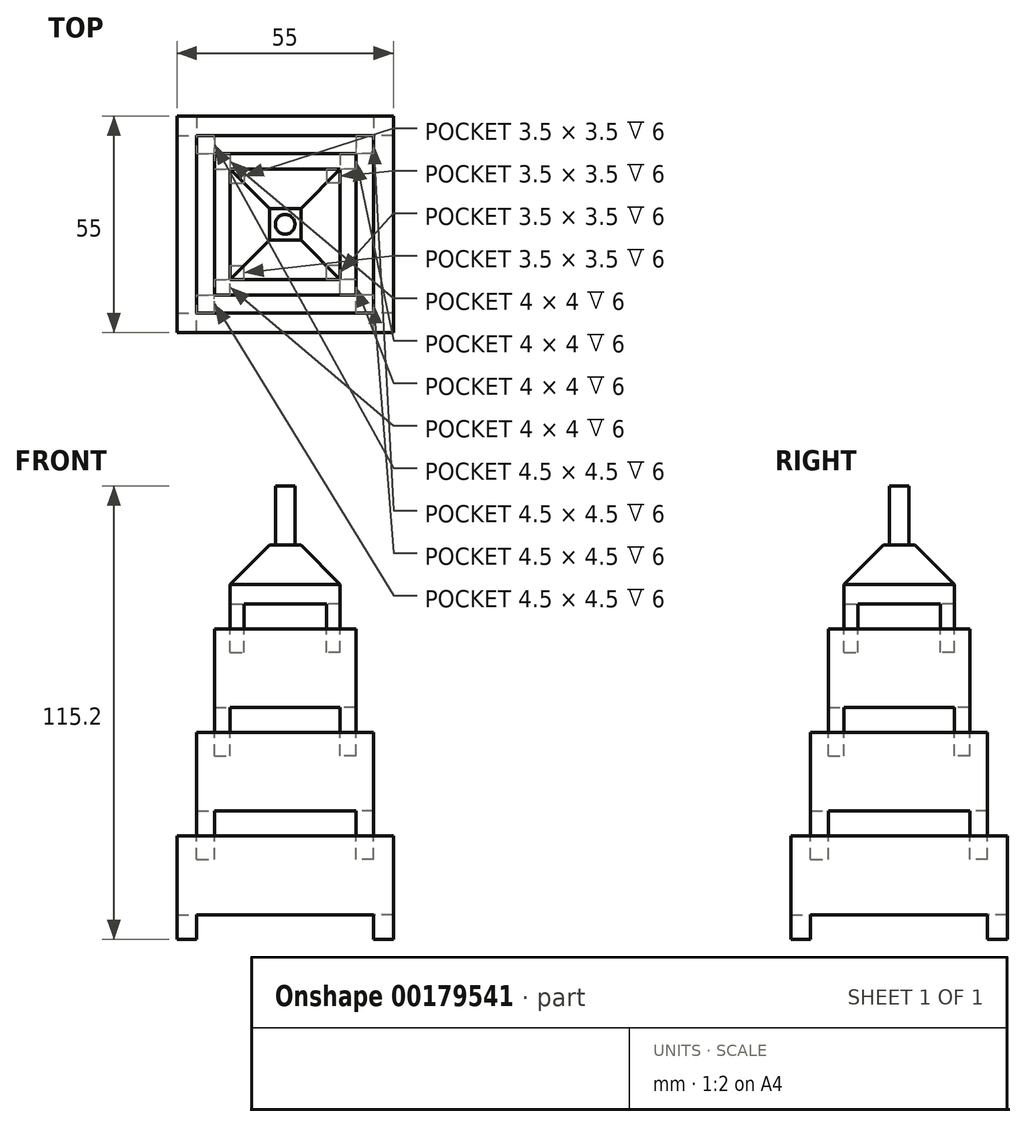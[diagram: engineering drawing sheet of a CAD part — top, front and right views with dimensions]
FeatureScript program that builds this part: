
annotation { "Feature Type Name" : "Feature", "Feature Type Description" : "" }
export const myFeature = defineFeature(function(context is Context, id is Id, definition is map)
    precondition{}
    {
        {
            var Q0;
            Q0=qCreatedBy(makeId("Top.planeOp"),FACE);
            var sketch = newSketch(context, id + "F0", { "sketchPlane" : qUnion([Q0])});
            skLineSegment(sketch, "E0.bottom", {"start": v(-40, 40) * mm, "end": v(40, 40) * mm});
            skLineSegment(sketch, "E0.top", {"start": v(-40, -40) * mm, "end": v(40, -40) * mm});
            skLineSegment(sketch, "E0.left", {"start": v(-40, 40) * mm, "end": v(-40, -40) * mm});
            skLineSegment(sketch, "E0.right", {"start": v(40, 40) * mm, "end": v(40, -40) * mm});
            skPoint(sketch, "E0.middle", {"position": v(0, 0) * mm});
            skLineSegment(sketch, "E1.bottom", {"start": v(-27.5, 27.5) * mm, "end": v(-22.5, 27.5) * mm});
            skLineSegment(sketch, "E1.top", {"start": v(-27.5, 22.5) * mm, "end": v(-22.5, 22.5) * mm});
            skLineSegment(sketch, "E1.left", {"start": v(-27.5, 27.5) * mm, "end": v(-27.5, 22.5) * mm});
            skLineSegment(sketch, "E1.right", {"start": v(-22.5, 27.5) * mm, "end": v(-22.5, 22.5) * mm});
            skPoint(sketch, "E1.middle", {"position": v(-25, 25) * mm});
            skLineSegment(sketch, "E2.bottom", {"start": v(-27.5, -27.5) * mm, "end": v(-22.5, -27.5) * mm});
            skLineSegment(sketch, "E2.top", {"start": v(-27.5, -22.5) * mm, "end": v(-22.5, -22.5) * mm});
            skLineSegment(sketch, "E2.left", {"start": v(-27.5, -27.5) * mm, "end": v(-27.5, -22.5) * mm});
            skLineSegment(sketch, "E2.right", {"start": v(-22.5, -27.5) * mm, "end": v(-22.5, -22.5) * mm});
            skPoint(sketch, "E2.middle", {"position": v(-25, -25) * mm});
            skLineSegment(sketch, "E3.bottom", {"start": v(27.5, -27.5) * mm, "end": v(22.5, -27.5) * mm});
            skLineSegment(sketch, "E3.top", {"start": v(27.5, -22.5) * mm, "end": v(22.5, -22.5) * mm});
            skLineSegment(sketch, "E3.left", {"start": v(27.5, -27.5) * mm, "end": v(27.5, -22.5) * mm});
            skLineSegment(sketch, "E3.right", {"start": v(22.5, -27.5) * mm, "end": v(22.5, -22.5) * mm});
            skPoint(sketch, "E3.middle", {"position": v(25, -25) * mm});
            skLineSegment(sketch, "E4.bottom", {"start": v(27.5, 27.5) * mm, "end": v(22.5, 27.5) * mm});
            skLineSegment(sketch, "E4.top", {"start": v(27.5, 22.5) * mm, "end": v(22.5, 22.5) * mm});
            skLineSegment(sketch, "E4.left", {"start": v(27.5, 27.5) * mm, "end": v(27.5, 22.5) * mm});
            skLineSegment(sketch, "E4.right", {"start": v(22.5, 27.5) * mm, "end": v(22.5, 22.5) * mm});
            skPoint(sketch, "E4.middle", {"position": v(25, 25) * mm});
            skSolve(sketch);
        }
        {
            var Q0;
            Q0=makeQuery(id+"F0.imprint","IMPRINT",FACE,{"disambiguationData":[TD([[makeQuery(id+"F0.imprint","IMPRINT",EDGE,{"derivedFrom":sQuery(id+"F0.wireOp",EDGE,"E4.bottom")}),1.0]])]});
            var Q1;
            Q1=makeQuery(id+"F0.imprint","IMPRINT",FACE,{"disambiguationData":[TD([[makeQuery(id+"F0.imprint","IMPRINT",EDGE,{"derivedFrom":sQuery(id+"F0.wireOp",EDGE,"E1.bottom")}),-1.0]])]});
            var Q2;
            Q2=makeQuery(id+"F0.imprint","IMPRINT",FACE,{"disambiguationData":[TD([[makeQuery(id+"F0.imprint","IMPRINT",EDGE,{"derivedFrom":sQuery(id+"F0.wireOp",EDGE,"E2.bottom")}),1.0]])]});
            var Q3;
            Q3=makeQuery(id+"F0.imprint","IMPRINT",FACE,{"disambiguationData":[TD([[makeQuery(id+"F0.imprint","IMPRINT",EDGE,{"derivedFrom":sQuery(id+"F0.wireOp",EDGE,"E3.bottom")}),-1.0]])]});
            extrude(context, id + "F1", {"entities" : qUnion([Q0, Q1, Q2, Q3]), "depth" : 6.3 * mm});
        }
        {
            var Q0;
            Q0=makeQuery(id+"F1.opExtrude","CAP_FACE",FACE,{"disambiguationData":[OSD([sQuery(id+"F0.wireOp",EDGE,"E4.bottom"),sQuery(id+"F0.wireOp",EDGE,"E4.top"),sQuery(id+"F0.wireOp",EDGE,"E4.left"),sQuery(id+"F0.wireOp",EDGE,"E4.right")])],"isStart":false});
            var sketch = newSketch(context, id + "F2", { "sketchPlane" : qUnion([Q0])});
            skLineSegment(sketch, "E5.bottom", {"start": v(27.5, 27.5) * mm, "end": v(-27.5, 27.5) * mm});
            skLineSegment(sketch, "E5.top", {"start": v(27.5, -27.5) * mm, "end": v(-27.5, -27.5) * mm});
            skLineSegment(sketch, "E5.left", {"start": v(27.5, 27.5) * mm, "end": v(27.5, -27.5) * mm});
            skLineSegment(sketch, "E5.right", {"start": v(-27.5, 27.5) * mm, "end": v(-27.5, -27.5) * mm});
            skSolve(sketch);
        }
        {
            var Q0;
            {var subQ3=sQuery(id+"F2.wireOp",EDGE,"E5.top");Q0=makeQuery(id+"F2.imprint","IMPRINT",FACE,{"disambiguationData":[TD([[makeQuery(id+"F2.imprint","IMPRINT",EDGE,{"derivedFrom":subQ3}),-1.0]])]});}
            var Q1;
            {var subQ4=makeQuery(id+"F1.opExtrude","CAP_EDGE",EDGE,{"disambiguationData":[OSD([sQuery(id+"F0.wireOp",EDGE,"E4.top")])],"isStart":false});Q1=makeQuery(id+"F2.imprint","IMPRINT",FACE,{"disambiguationData":[TD([[makeQuery(id+"F2.imprint","IMPRINT",EDGE,{"derivedFrom":subQ4}),-1.0]])]});}
            extrude(context, id + "F3", {"entities" : qUnion([Q0, Q1]), "operationType" : NewBodyOperationType.ADD, "depth" : 20 * mm});
        }
        {
            var Q0;
            Q0=makeQuery(id+"F3.opExtrude","CAP_FACE",FACE,{"disambiguationData":[OSD([sQuery(id+"F2.wireOp",EDGE,"E5.bottom"),sQuery(id+"F2.wireOp",EDGE,"E5.top"),sQuery(id+"F2.wireOp",EDGE,"E5.left"),sQuery(id+"F2.wireOp",EDGE,"E5.right")])],"isStart":false});
            var sketch = newSketch(context, id + "F4", { "sketchPlane" : qUnion([Q0])});
            skLineSegment(sketch, "E6.0", {"start": v(-27.5, -27.5) * mm, "end": v(-22.5, -27.5) * mm});
            skLineSegment(sketch, "E6.1", {"start": v(-27.5, 27.5) * mm, "end": v(-27.5, 22.5) * mm});
            skLineSegment(sketch, "E6.2", {"start": v(-27.5, -27.5) * mm, "end": v(-27.5, -22.5) * mm});
            skLineSegment(sketch, "E6.3", {"start": v(-27.5, 27.5) * mm, "end": v(-22.5, 27.5) * mm});
            skLineSegment(sketch, "E6.4", {"start": v(27.5, -27.5) * mm, "end": v(22.5, -27.5) * mm});
            skLineSegment(sketch, "E6.5", {"start": v(-22.5, -27.5) * mm, "end": v(-22.5, -22.5) * mm});
            skLineSegment(sketch, "E6.6", {"start": v(27.5, 27.5) * mm, "end": v(22.5, 27.5) * mm});
            skLineSegment(sketch, "E6.7", {"start": v(-22.5, 27.5) * mm, "end": v(-22.5, 22.5) * mm});
            skLineSegment(sketch, "E6.8", {"start": v(27.5, -27.5) * mm, "end": v(27.5, -22.5) * mm});
            skLineSegment(sketch, "E6.9", {"start": v(27.5, 27.5) * mm, "end": v(27.5, 22.5) * mm});
            skLineSegment(sketch, "E6.10", {"start": v(27.5, 27.5) * mm, "end": v(-27.5, 27.5) * mm});
            skLineSegment(sketch, "E6.11", {"start": v(27.5, -27.5) * mm, "end": v(-27.5, -27.5) * mm});
            skLineSegment(sketch, "E6.12", {"start": v(27.5, 22.5) * mm, "end": v(22.5, 22.5) * mm});
            skLineSegment(sketch, "E6.13", {"start": v(27.5, -22.5) * mm, "end": v(22.5, -22.5) * mm});
            skLineSegment(sketch, "E6.14", {"start": v(-27.5, 22.5) * mm, "end": v(-22.5, 22.5) * mm});
            skLineSegment(sketch, "E6.15", {"start": v(22.5, -27.5) * mm, "end": v(22.5, -22.5) * mm});
            skLineSegment(sketch, "E6.16", {"start": v(-27.5, -22.5) * mm, "end": v(-22.5, -22.5) * mm});
            skLineSegment(sketch, "E6.17", {"start": v(22.5, 27.5) * mm, "end": v(22.5, 22.5) * mm});
            skLineSegment(sketch, "E6.18", {"start": v(-27.5, 27.5) * mm, "end": v(-27.5, -27.5) * mm});
            skLineSegment(sketch, "E6.19", {"start": v(27.5, 27.5) * mm, "end": v(27.5, -27.5) * mm});
            skLineSegment(sketch, "E6.20", {"start": v(22.5, 27.5) * mm, "end": v(-22.5, 27.5) * mm});
            skLineSegment(sketch, "E6.21", {"start": v(22.5, -27.5) * mm, "end": v(-22.5, -27.5) * mm});
            skLineSegment(sketch, "E6.22", {"start": v(27.5, -27.5) * mm, "end": v(22.5, -27.5) * mm});
            skLineSegment(sketch, "E6.23", {"start": v(-22.5, -27.5) * mm, "end": v(-22.5, -22.5) * mm});
            skLineSegment(sketch, "E6.24", {"start": v(-22.5, 27.5) * mm, "end": v(-22.5, 22.5) * mm});
            skLineSegment(sketch, "E6.25", {"start": v(-27.5, 27.5) * mm, "end": v(-22.5, 27.5) * mm});
            skLineSegment(sketch, "E6.26", {"start": v(-27.5, -27.5) * mm, "end": v(-22.5, -27.5) * mm});
            skLineSegment(sketch, "E6.27", {"start": v(27.5, 27.5) * mm, "end": v(22.5, 27.5) * mm});
            skLineSegment(sketch, "E6.28", {"start": v(-27.5, 22.5) * mm, "end": v(-22.5, 22.5) * mm});
            skLineSegment(sketch, "E6.29", {"start": v(-27.5, -27.5) * mm, "end": v(-27.5, -22.5) * mm});
            skLineSegment(sketch, "E6.31", {"start": v(22.5, -27.5) * mm, "end": v(22.5, -22.5) * mm});
            skLineSegment(sketch, "E6.34", {"start": v(-22.5, -27.5) * mm, "end": v(-22.5, -22.5) * mm});
            skLineSegment(sketch, "E6.35", {"start": v(-22.5, 27.5) * mm, "end": v(-22.5, 22.5) * mm});
            skLineSegment(sketch, "E6.37", {"start": v(-27.5, 22.5) * mm, "end": v(-27.5, -22.5) * mm});
            skLineSegment(sketch, "E6.38", {"start": v(27.5, 22.5) * mm, "end": v(22.5, 22.5) * mm});
            skLineSegment(sketch, "E6.39", {"start": v(27.5, 22.5) * mm, "end": v(27.5, -22.5) * mm});
            skLineSegment(sketch, "E6.41", {"start": v(22.5, 27.5) * mm, "end": v(22.5, 22.5) * mm});
            skLineSegment(sketch, "E6.42", {"start": v(27.5, -22.5) * mm, "end": v(22.5, -22.5) * mm});
            skLineSegment(sketch, "E6.43", {"start": v(-27.5, -22.5) * mm, "end": v(-22.5, -22.5) * mm});
            skLineSegment(sketch, "E6.44", {"start": v(-27.5, 27.5) * mm, "end": v(-27.5, 22.5) * mm});
            skLineSegment(sketch, "E6.49", {"start": v(27.5, -27.5) * mm, "end": v(27.5, -22.5) * mm});
            skLineSegment(sketch, "E6.51", {"start": v(27.5, 27.5) * mm, "end": v(27.5, 22.5) * mm});
            skLineSegment(sketch, "E6.52", {"start": v(-27.5, 22.5) * mm, "end": v(-22.5, 22.5) * mm});
            skLineSegment(sketch, "E6.53", {"start": v(22.5, 27.5) * mm, "end": v(22.5, 22.5) * mm});
            skLineSegment(sketch, "E6.54", {"start": v(22.5, -27.5) * mm, "end": v(22.5, -22.5) * mm});
            skLineSegment(sketch, "E6.55", {"start": v(27.5, -22.5) * mm, "end": v(22.5, -22.5) * mm});
            skLineSegment(sketch, "E6.62", {"start": v(27.5, 22.5) * mm, "end": v(22.5, 22.5) * mm});
            skLineSegment(sketch, "E6.63", {"start": v(-27.5, -22.5) * mm, "end": v(-22.5, -22.5) * mm});
            skLineSegment(sketch, "E7.bottom", {"start": v(-22.5, 22.5) * mm, "end": v(-18, 22.5) * mm});
            skLineSegment(sketch, "E7.top", {"start": v(-22.5, 18) * mm, "end": v(-18, 18) * mm});
            skLineSegment(sketch, "E7.left", {"start": v(-22.5, 22.5) * mm, "end": v(-22.5, 18) * mm});
            skLineSegment(sketch, "E7.right", {"start": v(-18, 22.5) * mm, "end": v(-18, 18) * mm});
            skLineSegment(sketch, "E8.bottom", {"start": v(-22.5, -22.5) * mm, "end": v(-18, -22.5) * mm});
            skLineSegment(sketch, "E8.top", {"start": v(-22.5, -18) * mm, "end": v(-18, -18) * mm});
            skLineSegment(sketch, "E8.left", {"start": v(-22.5, -22.5) * mm, "end": v(-22.5, -18) * mm});
            skLineSegment(sketch, "E8.right", {"start": v(-18, -22.5) * mm, "end": v(-18, -18) * mm});
            skLineSegment(sketch, "E9.bottom", {"start": v(22.5, -22.5) * mm, "end": v(18, -22.5) * mm});
            skLineSegment(sketch, "E9.top", {"start": v(22.5, -18) * mm, "end": v(18, -18) * mm});
            skLineSegment(sketch, "E9.left", {"start": v(22.5, -22.5) * mm, "end": v(22.5, -18) * mm});
            skLineSegment(sketch, "E9.right", {"start": v(18, -22.5) * mm, "end": v(18, -18) * mm});
            skLineSegment(sketch, "E10.bottom", {"start": v(22.5, 22.5) * mm, "end": v(18, 22.5) * mm});
            skLineSegment(sketch, "E10.top", {"start": v(22.5, 18) * mm, "end": v(18, 18) * mm});
            skLineSegment(sketch, "E10.left", {"start": v(22.5, 22.5) * mm, "end": v(22.5, 18) * mm});
            skLineSegment(sketch, "E10.right", {"start": v(18, 22.5) * mm, "end": v(18, 18) * mm});
            skSolve(sketch);
        }
        {
            var Q0;
            Q0=makeQuery(id+"F4.imprint","IMPRINT",FACE,{"disambiguationData":[TD([[makeQuery(id+"F4.imprint","IMPRINT",EDGE,{"derivedFrom":sQuery(id+"F4.wireOp",EDGE,"E7.bottom")}),-1.0]])]});
            var Q1;
            Q1=makeQuery(id+"F4.imprint","IMPRINT",FACE,{"disambiguationData":[TD([[makeQuery(id+"F4.imprint","IMPRINT",EDGE,{"derivedFrom":sQuery(id+"F4.wireOp",EDGE,"E10.bottom")}),1.0]])]});
            var Q2;
            Q2=makeQuery(id+"F4.imprint","IMPRINT",FACE,{"disambiguationData":[TD([[makeQuery(id+"F4.imprint","IMPRINT",EDGE,{"derivedFrom":sQuery(id+"F4.wireOp",EDGE,"E9.bottom")}),-1.0]])]});
            var Q3;
            Q3=makeQuery(id+"F4.imprint","IMPRINT",FACE,{"disambiguationData":[TD([[makeQuery(id+"F4.imprint","IMPRINT",EDGE,{"derivedFrom":sQuery(id+"F4.wireOp",EDGE,"E8.bottom")}),1.0]])]});
            extrude(context, id + "F5", {"entities" : qUnion([Q0, Q1, Q2, Q3]), "depth" : 6.3 * mm});
        }
        {
            var Q0;
            Q0=makeQuery(id+"F5.opExtrude","CAP_FACE",FACE,{"disambiguationData":[OSD([sQuery(id+"F4.wireOp",EDGE,"E10.bottom"),sQuery(id+"F4.wireOp",EDGE,"E10.top"),sQuery(id+"F4.wireOp",EDGE,"E10.left"),sQuery(id+"F4.wireOp",EDGE,"E10.right")])],"isStart":false});
            var sketch = newSketch(context, id + "F6", { "sketchPlane" : qUnion([Q0])});
            skLineSegment(sketch, "E11.bottom", {"start": v(22.5, 22.5) * mm, "end": v(-22.5, 22.5) * mm});
            skLineSegment(sketch, "E11.top", {"start": v(22.5, -22.5) * mm, "end": v(-22.5, -22.5) * mm});
            skLineSegment(sketch, "E11.left", {"start": v(22.5, 22.5) * mm, "end": v(22.5, -22.5) * mm});
            skLineSegment(sketch, "E11.right", {"start": v(-22.5, 22.5) * mm, "end": v(-22.5, -22.5) * mm});
            skSolve(sketch);
        }
        {
            var Q0;
            Q0 = qSketchRegion(id + "F6", true);
            extrude(context, id + "F7", {"entities" : qUnion([Q0]), "operationType" : NewBodyOperationType.ADD, "depth" : 20 * mm});
        }
        {
            var Q0;
            Q0=makeQuery(id+"F7.opExtrude","CAP_FACE",FACE,{"disambiguationData":[OSD([sQuery(id+"F6.wireOp",EDGE,"E11.bottom"),sQuery(id+"F6.wireOp",EDGE,"E11.top"),sQuery(id+"F6.wireOp",EDGE,"E11.left"),sQuery(id+"F6.wireOp",EDGE,"E11.right")])],"isStart":false});
            var sketch = newSketch(context, id + "F8", { "sketchPlane" : qUnion([Q0])});
            skLineSegment(sketch, "E12.bottom", {"start": v(-18, 18) * mm, "end": v(-14, 18) * mm});
            skLineSegment(sketch, "E12.top", {"start": v(-18, 14) * mm, "end": v(-14, 14) * mm});
            skLineSegment(sketch, "E12.left", {"start": v(-18, 18) * mm, "end": v(-18, 14) * mm});
            skLineSegment(sketch, "E12.right", {"start": v(-14, 18) * mm, "end": v(-14, 14) * mm});
            skLineSegment(sketch, "E13.bottom", {"start": v(18, 18) * mm, "end": v(14, 18) * mm});
            skLineSegment(sketch, "E13.top", {"start": v(18, 14) * mm, "end": v(14, 14) * mm});
            skLineSegment(sketch, "E13.left", {"start": v(18, 18) * mm, "end": v(18, 14) * mm});
            skLineSegment(sketch, "E13.right", {"start": v(14, 18) * mm, "end": v(14, 14) * mm});
            skLineSegment(sketch, "E14.bottom", {"start": v(18, -18) * mm, "end": v(14, -18) * mm});
            skLineSegment(sketch, "E14.top", {"start": v(18, -14) * mm, "end": v(14, -14) * mm});
            skLineSegment(sketch, "E14.left", {"start": v(18, -18) * mm, "end": v(18, -14) * mm});
            skLineSegment(sketch, "E14.right", {"start": v(14, -18) * mm, "end": v(14, -14) * mm});
            skLineSegment(sketch, "E15.bottom", {"start": v(-18, -18) * mm, "end": v(-14, -18) * mm});
            skLineSegment(sketch, "E15.top", {"start": v(-18, -14) * mm, "end": v(-14, -14) * mm});
            skLineSegment(sketch, "E15.left", {"start": v(-18, -18) * mm, "end": v(-18, -14) * mm});
            skLineSegment(sketch, "E15.right", {"start": v(-14, -18) * mm, "end": v(-14, -14) * mm});
            skSolve(sketch);
        }
        {
            var Q0;
            Q0=makeQuery(id+"F8.imprint","IMPRINT",FACE,{"disambiguationData":[TD([[makeQuery(id+"F8.imprint","IMPRINT",EDGE,{"derivedFrom":sQuery(id+"F8.wireOp",EDGE,"E13.bottom")}),1.0]])]});
            var Q1;
            Q1=makeQuery(id+"F8.imprint","IMPRINT",FACE,{"disambiguationData":[TD([[makeQuery(id+"F8.imprint","IMPRINT",EDGE,{"derivedFrom":sQuery(id+"F8.wireOp",EDGE,"E14.bottom")}),-1.0]])]});
            var Q2;
            Q2=makeQuery(id+"F8.imprint","IMPRINT",FACE,{"disambiguationData":[TD([[makeQuery(id+"F8.imprint","IMPRINT",EDGE,{"derivedFrom":sQuery(id+"F8.wireOp",EDGE,"E15.bottom")}),1.0]])]});
            var Q3;
            Q3=makeQuery(id+"F8.imprint","IMPRINT",FACE,{"disambiguationData":[TD([[makeQuery(id+"F8.imprint","IMPRINT",EDGE,{"derivedFrom":sQuery(id+"F8.wireOp",EDGE,"E12.bottom")}),-1.0]])]});
            extrude(context, id + "F9", {"entities" : qUnion([Q0, Q1, Q2, Q3]), "depth" : 6.3 * mm});
        }
        {
            var Q0;
            Q0=makeQuery(id+"F9.opExtrude","CAP_FACE",FACE,{"disambiguationData":[OSD([sQuery(id+"F8.wireOp",EDGE,"E12.bottom"),sQuery(id+"F8.wireOp",EDGE,"E12.top"),sQuery(id+"F8.wireOp",EDGE,"E12.left"),sQuery(id+"F8.wireOp",EDGE,"E12.right")])],"isStart":false});
            var sketch = newSketch(context, id + "F10", { "sketchPlane" : qUnion([Q0])});
            skLineSegment(sketch, "E16.bottom", {"start": v(18, 18) * mm, "end": v(-18, 18) * mm});
            skLineSegment(sketch, "E16.top", {"start": v(18, -18) * mm, "end": v(-18, -18) * mm});
            skLineSegment(sketch, "E16.left", {"start": v(18, 18) * mm, "end": v(18, -18) * mm});
            skLineSegment(sketch, "E16.right", {"start": v(-18, 18) * mm, "end": v(-18, -18) * mm});
            skLineSegment(sketch, "E17.0", {"start": v(-18, 14) * mm, "end": v(-14, 14) * mm});
            skLineSegment(sketch, "E17.1", {"start": v(-14, 18) * mm, "end": v(-14, 14) * mm});
            skLineSegment(sketch, "E17.2", {"start": v(14, 18) * mm, "end": v(14, 14) * mm});
            skLineSegment(sketch, "E17.3", {"start": v(18, 14) * mm, "end": v(14, 14) * mm});
            skLineSegment(sketch, "E17.4", {"start": v(18, -14) * mm, "end": v(14, -14) * mm});
            skLineSegment(sketch, "E17.5", {"start": v(14, -18) * mm, "end": v(14, -14) * mm});
            skLineSegment(sketch, "E17.6", {"start": v(-14, -18) * mm, "end": v(-14, -14) * mm});
            skLineSegment(sketch, "E17.7", {"start": v(-18, -14) * mm, "end": v(-14, -14) * mm});
            skSolve(sketch);
        }
        {
            var Q0;
            Q0 = qSketchRegion(id + "F10", true);
            extrude(context, id + "F11", {"entities" : qUnion([Q0]), "operationType" : NewBodyOperationType.ADD, "depth" : 20 * mm});
        }
        {
            var Q0;
            Q0=makeQuery(id+"F11.opExtrude","CAP_FACE",FACE,{"disambiguationData":[OSD([sQuery(id+"F10.wireOp",EDGE,"E16.bottom"),sQuery(id+"F10.wireOp",EDGE,"E16.top"),sQuery(id+"F10.wireOp",EDGE,"E16.left"),sQuery(id+"F10.wireOp",EDGE,"E16.right")])],"isStart":false});
            var sketch = newSketch(context, id + "F12", { "sketchPlane" : qUnion([Q0])});
            skLineSegment(sketch, "E18.0", {"start": v(-14, 18) * mm, "end": v(-14, 14) * mm});
            skLineSegment(sketch, "E18.1", {"start": v(-18, 14) * mm, "end": v(-14, 14) * mm});
            skLineSegment(sketch, "E18.2", {"start": v(14, 18) * mm, "end": v(14, 14) * mm});
            skLineSegment(sketch, "E18.3", {"start": v(18, 14) * mm, "end": v(14, 14) * mm});
            skLineSegment(sketch, "E18.4", {"start": v(18, -14) * mm, "end": v(14, -14) * mm});
            skLineSegment(sketch, "E18.5", {"start": v(14, -18) * mm, "end": v(14, -14) * mm});
            skLineSegment(sketch, "E18.6", {"start": v(-14, -18) * mm, "end": v(-14, -14) * mm});
            skLineSegment(sketch, "E18.7", {"start": v(-18, -14) * mm, "end": v(-14, -14) * mm});
            skLineSegment(sketch, "E19.bottom", {"start": v(-14, 14) * mm, "end": v(-10.5, 14) * mm});
            skLineSegment(sketch, "E19.top", {"start": v(-14, 10.5) * mm, "end": v(-10.5, 10.5) * mm});
            skLineSegment(sketch, "E19.left", {"start": v(-14, 14) * mm, "end": v(-14, 10.5) * mm});
            skLineSegment(sketch, "E19.right", {"start": v(-10.5, 14) * mm, "end": v(-10.5, 10.5) * mm});
            skLineSegment(sketch, "E20.bottom", {"start": v(14, 14) * mm, "end": v(10.5, 14) * mm});
            skLineSegment(sketch, "E20.top", {"start": v(14, 10.5) * mm, "end": v(10.5, 10.5) * mm});
            skLineSegment(sketch, "E20.left", {"start": v(14, 14) * mm, "end": v(14, 10.5) * mm});
            skLineSegment(sketch, "E20.right", {"start": v(10.5, 14) * mm, "end": v(10.5, 10.5) * mm});
            skLineSegment(sketch, "E21.bottom", {"start": v(14, -14) * mm, "end": v(10.5, -14) * mm});
            skLineSegment(sketch, "E21.top", {"start": v(14, -10.5) * mm, "end": v(10.5, -10.5) * mm});
            skLineSegment(sketch, "E21.left", {"start": v(14, -14) * mm, "end": v(14, -10.5) * mm});
            skLineSegment(sketch, "E21.right", {"start": v(10.5, -14) * mm, "end": v(10.5, -10.5) * mm});
            skLineSegment(sketch, "E22.bottom", {"start": v(-14, -14) * mm, "end": v(-10.5, -14) * mm});
            skLineSegment(sketch, "E22.top", {"start": v(-14, -10.5) * mm, "end": v(-10.5, -10.5) * mm});
            skLineSegment(sketch, "E22.left", {"start": v(-14, -14) * mm, "end": v(-14, -10.5) * mm});
            skLineSegment(sketch, "E22.right", {"start": v(-10.5, -14) * mm, "end": v(-10.5, -10.5) * mm});
            skSolve(sketch);
        }
        {
            var Q0;
            Q0=makeQuery(id+"F12.imprint","IMPRINT",FACE,{"disambiguationData":[TD([[makeQuery(id+"F12.imprint","IMPRINT",EDGE,{"derivedFrom":sQuery(id+"F12.wireOp",EDGE,"E19.bottom")}),-1.0]])]});
            var Q1;
            Q1=makeQuery(id+"F12.imprint","IMPRINT",FACE,{"disambiguationData":[TD([[makeQuery(id+"F12.imprint","IMPRINT",EDGE,{"derivedFrom":sQuery(id+"F12.wireOp",EDGE,"E20.bottom")}),1.0]])]});
            var Q2;
            Q2=makeQuery(id+"F12.imprint","IMPRINT",FACE,{"disambiguationData":[TD([[makeQuery(id+"F12.imprint","IMPRINT",EDGE,{"derivedFrom":sQuery(id+"F12.wireOp",EDGE,"E21.bottom")}),-1.0]])]});
            var Q3;
            Q3=makeQuery(id+"F12.imprint","IMPRINT",FACE,{"disambiguationData":[TD([[makeQuery(id+"F12.imprint","IMPRINT",EDGE,{"derivedFrom":sQuery(id+"F12.wireOp",EDGE,"E22.bottom")}),1.0]])]});
            extrude(context, id + "F13", {"entities" : qUnion([Q0, Q1, Q2, Q3]), "operationType" : NewBodyOperationType.ADD, "depth" : 6.3 * mm});
        }
        {
            var Q0;
            Q0=makeQuery(id+"F13.opExtrude","CAP_FACE",FACE,{"disambiguationData":[OSD([sQuery(id+"F12.wireOp",EDGE,"E20.bottom"),sQuery(id+"F12.wireOp",EDGE,"E20.top"),sQuery(id+"F12.wireOp",EDGE,"E20.left"),sQuery(id+"F12.wireOp",EDGE,"E20.right")])],"isStart":false});
            var sketch = newSketch(context, id + "F14", { "sketchPlane" : qUnion([Q0])});
            skLineSegment(sketch, "E23.bottom", {"start": v(14, 14) * mm, "end": v(-14, 14) * mm});
            skLineSegment(sketch, "E23.top", {"start": v(14, -14) * mm, "end": v(-14, -14) * mm});
            skLineSegment(sketch, "E23.left", {"start": v(14, 14) * mm, "end": v(14, -14) * mm});
            skLineSegment(sketch, "E23.right", {"start": v(-14, 14) * mm, "end": v(-14, -14) * mm});
            skSolve(sketch);
        }
        {
            var Q0;
            {var subQ3=sQuery(id+"F14.wireOp",EDGE,"E23.top");Q0=makeQuery(id+"F14.imprint","IMPRINT",FACE,{"disambiguationData":[TD([[makeQuery(id+"F14.imprint","IMPRINT",EDGE,{"derivedFrom":subQ3}),-1.0]])]});}
            var Q1;
            {var subQ4=makeQuery(id+"F13.opExtrude","CAP_EDGE",EDGE,{"disambiguationData":[OSD([sQuery(id+"F12.wireOp",EDGE,"E20.top")])],"isStart":false});Q1=makeQuery(id+"F14.imprint","IMPRINT",FACE,{"disambiguationData":[TD([[makeQuery(id+"F14.imprint","IMPRINT",EDGE,{"derivedFrom":subQ4}),-1.0]])]});}
            extrude(context, id + "F15", {"entities" : qUnion([Q0, Q1]), "operationType" : NewBodyOperationType.ADD, "depth" : 15 * mm});
        }
        {
            var Q0;
            Q0=makeQuery(id+"F15.opExtrude","CAP_EDGE",EDGE,{"disambiguationData":[OSD([sQuery(id+"F14.wireOp",EDGE,"E23.top")])],"isStart":false});
            var Q1;
            Q1=makeQuery(id+"F15.opExtrude","CAP_EDGE",EDGE,{"disambiguationData":[OSD([sQuery(id+"F14.wireOp",EDGE,"E23.right")])],"isStart":false});
            var Q2;
            Q2=makeQuery(id+"F15.opExtrude","CAP_EDGE",EDGE,{"disambiguationData":[OSD([sQuery(id+"F14.wireOp",EDGE,"E23.bottom")])],"isStart":false});
            var Q3;
            Q3=makeQuery(id+"F15.opExtrude","CAP_EDGE",EDGE,{"disambiguationData":[OSD([sQuery(id+"F14.wireOp",EDGE,"E23.left")])],"isStart":false});
            chamfer(context, id + "F16", {"entities" : qUnion([Q0, Q1, Q2, Q3]), "width" : 10 * mm, "tangentPropagation" : true});
        }
        {
            var Q0;
            Q0=makeQuery(id+"F15.opExtrude","CAP_FACE",FACE,{"disambiguationData":[OSD([sQuery(id+"F14.wireOp",EDGE,"E23.bottom"),sQuery(id+"F14.wireOp",EDGE,"E23.top"),sQuery(id+"F14.wireOp",EDGE,"E23.left"),sQuery(id+"F14.wireOp",EDGE,"E23.right")])],"isStart":false});
            var sketch = newSketch(context, id + "F17", { "sketchPlane" : qUnion([Q0])});
            skCircle(sketch, "E24", {"center": v(0, 0) * mm, "radius": 2.5 * mm});
            skSolve(sketch);
        }
        {
            var Q0;
            Q0=makeQuery(id+"F17.imprint","IMPRINT",FACE,{"disambiguationData":[TD([[makeQuery(id+"F17.imprint","IMPRINT",EDGE,{"derivedFrom":sQuery(id+"F17.wireOp",EDGE,"E24")}),1.0]])]});
            extrude(context, id + "F18", {"entities" : qUnion([Q0]), "operationType" : NewBodyOperationType.ADD, "depth" : 15 * mm});
        }
        {
            var Q0;
            Q0 = qSketchRegion(id + "F8", true);
            extrude(context, id + "F19", {"entities" : qUnion([Q0]), "operationType" : NewBodyOperationType.REMOVE, "oppositeDirection" : true, "depth" : 6 * mm});
        }
        {
            var Q0;
            Q0 = qSketchRegion(id + "F12", true);
            extrude(context, id + "F20", {"entities" : qUnion([Q0]), "operationType" : NewBodyOperationType.REMOVE, "oppositeDirection" : true, "depth" : 6 * mm});
        }
        {
            var Q0;
            Q0=makeQuery(id+"F4.imprint","IMPRINT",FACE,{"disambiguationData":[TD([[makeQuery(id+"F4.imprint","IMPRINT",EDGE,{"derivedFrom":sQuery(id+"F4.wireOp",EDGE,"E7.bottom")}),-1.0]])]});
            var Q1;
            Q1=makeQuery(id+"F4.imprint","IMPRINT",FACE,{"disambiguationData":[TD([[makeQuery(id+"F4.imprint","IMPRINT",EDGE,{"derivedFrom":sQuery(id+"F4.wireOp",EDGE,"E10.bottom")}),1.0]])]});
            var Q2;
            Q2=makeQuery(id+"F4.imprint","IMPRINT",FACE,{"disambiguationData":[TD([[makeQuery(id+"F4.imprint","IMPRINT",EDGE,{"derivedFrom":sQuery(id+"F4.wireOp",EDGE,"E9.bottom")}),-1.0]])]});
            var Q3;
            Q3=makeQuery(id+"F4.imprint","IMPRINT",FACE,{"disambiguationData":[TD([[makeQuery(id+"F4.imprint","IMPRINT",EDGE,{"derivedFrom":sQuery(id+"F4.wireOp",EDGE,"E8.bottom")}),1.0]])]});
            extrude(context, id + "F21", {"entities" : qUnion([Q0, Q1, Q2, Q3]), "operationType" : NewBodyOperationType.REMOVE, "oppositeDirection" : true, "depth" : 6 * mm});
        }
    });
